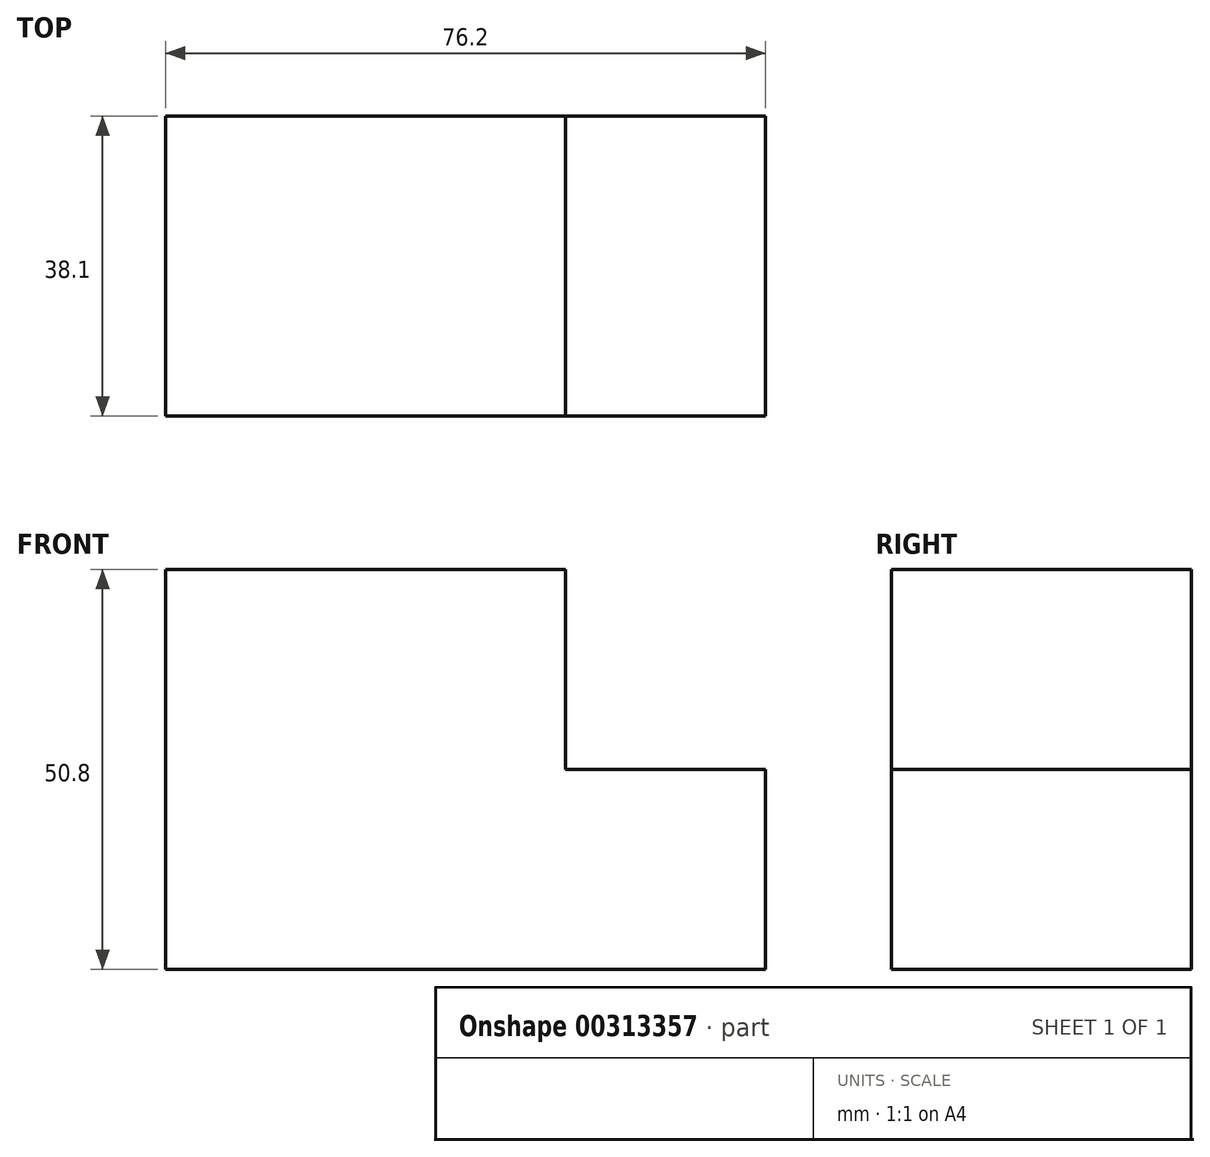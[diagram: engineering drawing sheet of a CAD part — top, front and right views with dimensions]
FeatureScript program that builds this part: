
annotation { "Feature Type Name" : "Feature", "Feature Type Description" : "" }
export const myFeature = defineFeature(function(context is Context, id is Id, definition is map)
    precondition{}
    {
        {
            var Q0;
            Q0=qCreatedBy(makeId("Front.planeOp"),FACE);
            var sketch = newSketch(context, id + "F0", { "sketchPlane" : qUnion([Q0])});
            skLineSegment(sketch, "E0", {"start": v(-34.5, -36.2) * mm, "end": v(41.7, -36.2) * mm});
            skLineSegment(sketch, "E1", {"start": v(41.7, -36.2) * mm, "end": v(41.7, -10.8) * mm});
            skLineSegment(sketch, "E2", {"start": v(41.7, -10.8) * mm, "end": v(16.3, -10.8) * mm});
            skLineSegment(sketch, "E3", {"start": v(16.3, -10.8) * mm, "end": v(16.3, 14.6) * mm});
            skLineSegment(sketch, "E4", {"start": v(16.3, 14.6) * mm, "end": v(-34.5, 14.6) * mm});
            skLineSegment(sketch, "E5", {"start": v(-34.5, 14.6) * mm, "end": v(-34.5, -36.2) * mm});
            skSolve(sketch);
        }
        {
            var Q0;
            Q0 = qSketchRegion(id + "F0", true);
            extrude(context, id + "F1", {"entities" : qUnion([Q0]), "depth" : 38.1 * mm});
        }
    });
